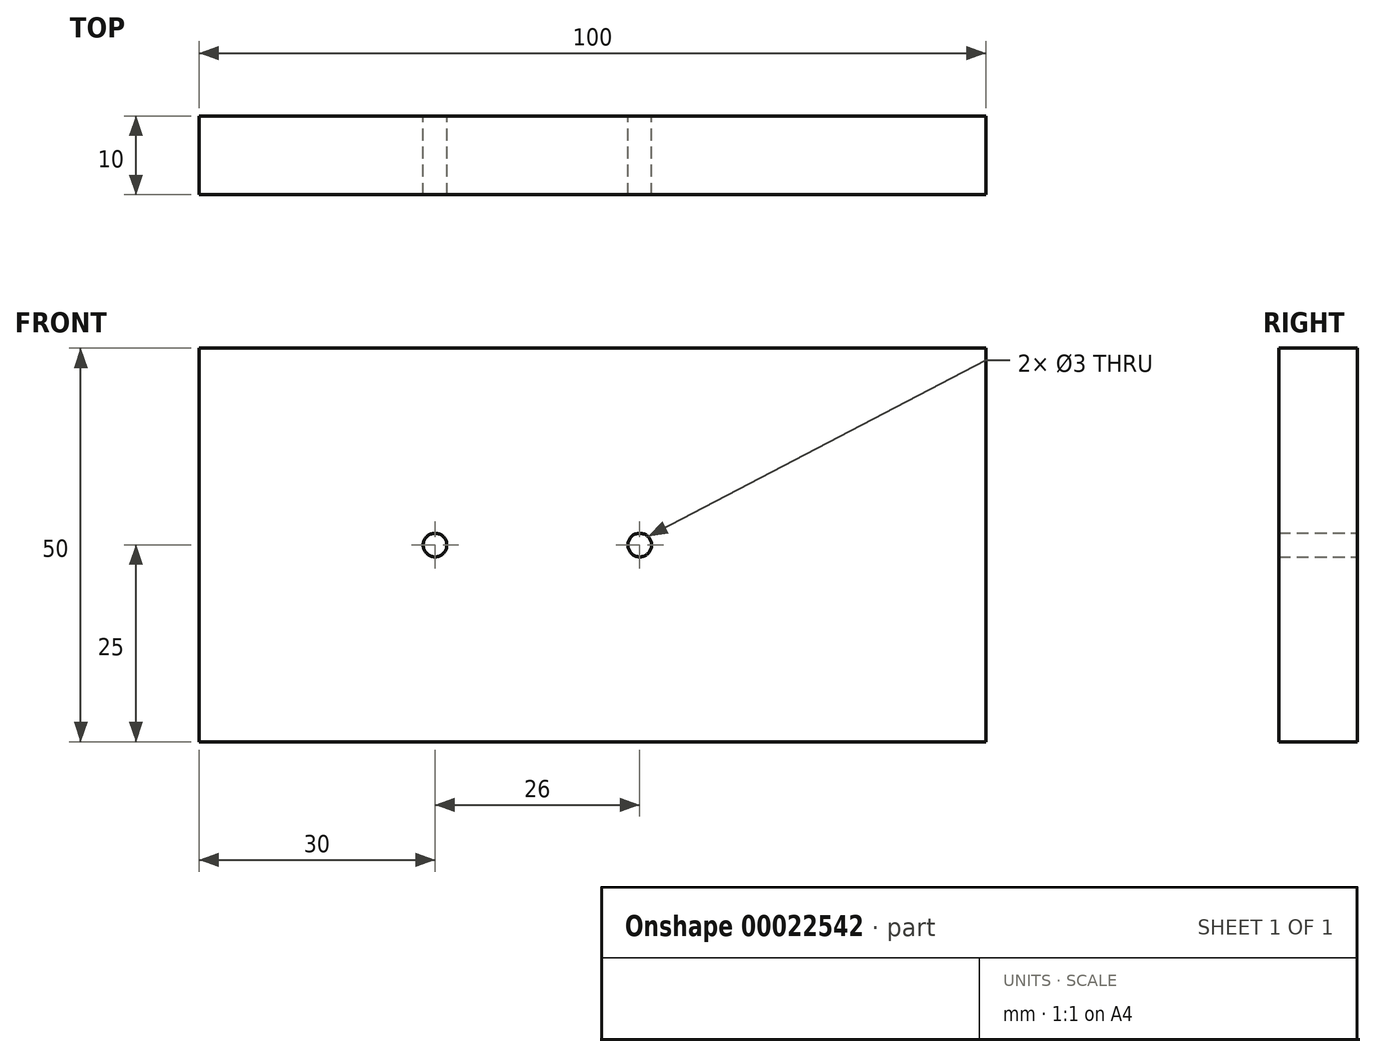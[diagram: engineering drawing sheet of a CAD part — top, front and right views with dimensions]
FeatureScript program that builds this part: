
annotation { "Feature Type Name" : "Feature", "Feature Type Description" : "" }
export const myFeature = defineFeature(function(context is Context, id is Id, definition is map)
    precondition{}
    {
        {
            var Q0;
            Q0=qCreatedBy(makeId("Front.planeOp"),FACE);
            var sketch = newSketch(context, id + "F0", { "sketchPlane" : qUnion([Q0])});
            skLineSegment(sketch, "E0.bottom", {"start": v(-50, 25) * mm, "end": v(50, 25) * mm});
            skLineSegment(sketch, "E0.top", {"start": v(-50, -25) * mm, "end": v(50, -25) * mm});
            skLineSegment(sketch, "E0.left", {"start": v(-50, 25) * mm, "end": v(-50, -25) * mm});
            skLineSegment(sketch, "E0.right", {"start": v(50, 25) * mm, "end": v(50, -25) * mm});
            skLineSegment(sketch, "E1", {"start": v(0, 0) * mm, "end": v(0, -25) * mm});
            skLineSegment(sketch, "E2", {"start": v(0, 0) * mm, "end": v(0, 25) * mm});
            skLineSegment(sketch, "E3", {"start": v(0, 0) * mm, "end": v(50, 0) * mm});
            skLineSegment(sketch, "E4", {"start": v(0, 0) * mm, "end": v(-50, 0) * mm});
            skLineSegment(sketch, "E5", {"start": v(-50, 25) * mm, "end": v(0, 25) * mm});
            skCircle(sketch, "E6", {"center": v(-20, 0) * mm, "radius": 1.5 * mm});
            skCircle(sketch, "E7", {"center": v(6, 0) * mm, "radius": 1.5 * mm});
            skLineSegment(sketch, "E8", {"start": v(-50, -25) * mm, "end": v(-50, 25) * mm});
            skLineSegment(sketch, "E9", {"start": v(0, 0) * mm, "end": v(-20, 0) * mm});
            skLineSegment(sketch, "E10", {"start": v(0, 0) * mm, "end": v(6, 0) * mm});
            skLineSegment(sketch, "E11", {"start": v(50, -25) * mm, "end": v(50, 25) * mm});
            skLineSegment(sketch, "E12", {"start": v(50, -25) * mm, "end": v(-50, -25) * mm});
            skLineSegment(sketch, "E13", {"start": v(6, 0) * mm, "end": v(0, 0) * mm});
            skLineSegment(sketch, "E14", {"start": v(-20, 0) * mm, "end": v(0, 0) * mm});
            skLineSegment(sketch, "E15", {"start": v(-20, 0) * mm, "end": v(-50, 0) * mm});
            skSolve(sketch);
        }
        {
            var Q0;
            {var subQ3=sQuery(id+"F0.wireOp",EDGE,"E2");Q0=makeQuery(id+"F0.imprint","IMPRINT",FACE,{"disambiguationData":[TD([[makeQuery(id+"F0.imprint","IMPRINT",EDGE,{"derivedFrom":subQ3}),1.0]])]});}
            var Q1;
            {var subQ3=sQuery(id+"F0.wireOp",EDGE,"E2");Q1=makeQuery(id+"F0.imprint","IMPRINT",FACE,{"disambiguationData":[TD([[makeQuery(id+"F0.imprint","IMPRINT",EDGE,{"derivedFrom":subQ3}),-1.0]])]});}
            var Q2;
            {var subQ5=sQuery(id+"F0.wireOp",EDGE,"E1");Q2=makeQuery(id+"F0.imprint","IMPRINT",FACE,{"disambiguationData":[TD([[makeQuery(id+"F0.imprint","IMPRINT",EDGE,{"derivedFrom":subQ5}),1.0]])]});}
            var Q3;
            {var subQ3=sQuery(id+"F0.wireOp",EDGE,"E1");Q3=makeQuery(id+"F0.imprint","IMPRINT",FACE,{"disambiguationData":[TD([[makeQuery(id+"F0.imprint","IMPRINT",EDGE,{"derivedFrom":subQ3}),-1.0]])]});}
            extrude(context, id + "F1", {"entities" : qUnion([Q0, Q1, Q2, Q3]), "depth" : 10 * mm});
        }
    });
